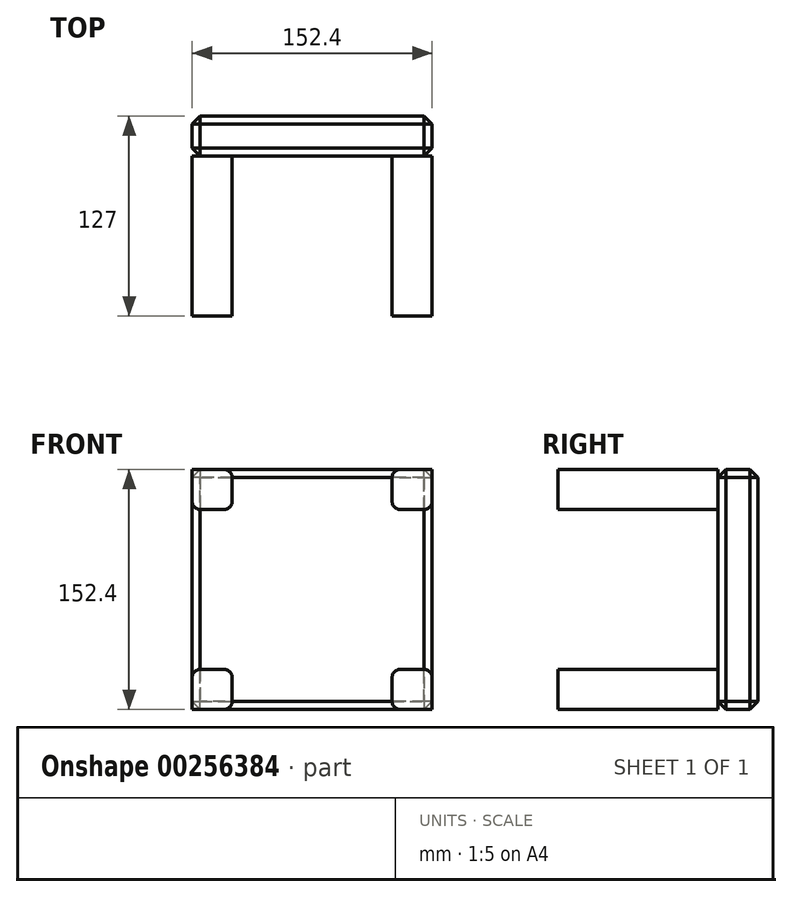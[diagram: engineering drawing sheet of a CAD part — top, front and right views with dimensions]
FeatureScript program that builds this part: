
annotation { "Feature Type Name" : "Feature", "Feature Type Description" : "" }
export const myFeature = defineFeature(function(context is Context, id is Id, definition is map)
    precondition{}
    {
        {
            var Q0;
            Q0=qCreatedBy(makeId("Front.planeOp"),FACE);
            var sketch = newSketch(context, id + "F0", { "sketchPlane" : qUnion([Q0])});
            skLineSegment(sketch, "E0.bottom", {"start": v(-76.2, 76.2) * mm, "end": v(-50.8, 76.2) * mm});
            skLineSegment(sketch, "E0.top", {"start": v(-76.2, 50.8) * mm, "end": v(-50.8, 50.8) * mm});
            skLineSegment(sketch, "E0.left", {"start": v(-76.2, 76.2) * mm, "end": v(-76.2, 50.8) * mm});
            skLineSegment(sketch, "E0.right", {"start": v(-50.8, 76.2) * mm, "end": v(-50.8, 50.8) * mm});
            skLineSegment(sketch, "E1.bottom", {"start": v(76.2, 76.2) * mm, "end": v(50.8, 76.2) * mm});
            skLineSegment(sketch, "E1.top", {"start": v(76.2, 50.8) * mm, "end": v(50.8, 50.8) * mm});
            skLineSegment(sketch, "E1.left", {"start": v(76.2, 76.2) * mm, "end": v(76.2, 50.8) * mm});
            skLineSegment(sketch, "E1.right", {"start": v(50.8, 76.2) * mm, "end": v(50.8, 50.8) * mm});
            skLineSegment(sketch, "E2.bottom", {"start": v(76.2, -76.2) * mm, "end": v(50.8, -76.2) * mm});
            skLineSegment(sketch, "E2.top", {"start": v(76.2, -50.8) * mm, "end": v(50.8, -50.8) * mm});
            skLineSegment(sketch, "E2.left", {"start": v(76.2, -76.2) * mm, "end": v(76.2, -50.8) * mm});
            skLineSegment(sketch, "E2.right", {"start": v(50.8, -76.2) * mm, "end": v(50.8, -50.8) * mm});
            skLineSegment(sketch, "E3.bottom", {"start": v(-76.2, -76.2) * mm, "end": v(-50.8, -76.2) * mm});
            skLineSegment(sketch, "E3.top", {"start": v(-76.2, -50.8) * mm, "end": v(-50.8, -50.8) * mm});
            skLineSegment(sketch, "E3.left", {"start": v(-76.2, -76.2) * mm, "end": v(-76.2, -50.8) * mm});
            skLineSegment(sketch, "E3.right", {"start": v(-50.8, -76.2) * mm, "end": v(-50.8, -50.8) * mm});
            skLineSegment(sketch, "E4.bottom", {"start": v(76.2, 76.2) * mm, "end": v(-76.2, 76.2) * mm});
            skLineSegment(sketch, "E4.top", {"start": v(76.2, -76.2) * mm, "end": v(-76.2, -76.2) * mm});
            skLineSegment(sketch, "E4.left", {"start": v(76.2, 76.2) * mm, "end": v(76.2, -76.2) * mm});
            skLineSegment(sketch, "E4.right", {"start": v(-76.2, 76.2) * mm, "end": v(-76.2, -76.2) * mm});
            skPoint(sketch, "E4.middle", {"position": v(0, 0) * mm});
            skSolve(sketch);
        }
        {
            var Q0;
            {var subQ0=sQuery(id+"F0.wireOp",EDGE,"E0.top");Q0=makeQuery(id+"F0.imprint","IMPRINT",FACE,{"disambiguationData":[TD([[makeQuery(id+"F0.imprint","IMPRINT",EDGE,{"derivedFrom":subQ0}),1.0]])]});}
            var Q1;
            {var subQ0=sQuery(id+"F0.wireOp",EDGE,"E1.top");Q1=makeQuery(id+"F0.imprint","IMPRINT",FACE,{"disambiguationData":[TD([[makeQuery(id+"F0.imprint","IMPRINT",EDGE,{"derivedFrom":subQ0}),-1.0]])]});}
            var Q2;
            {var subQ0=sQuery(id+"F0.wireOp",EDGE,"E2.top");Q2=makeQuery(id+"F0.imprint","IMPRINT",FACE,{"disambiguationData":[TD([[makeQuery(id+"F0.imprint","IMPRINT",EDGE,{"derivedFrom":subQ0}),1.0]])]});}
            var Q3;
            {var subQ0=sQuery(id+"F0.wireOp",EDGE,"E3.top");Q3=makeQuery(id+"F0.imprint","IMPRINT",FACE,{"disambiguationData":[TD([[makeQuery(id+"F0.imprint","IMPRINT",EDGE,{"derivedFrom":subQ0}),-1.0]])]});}
            extrude(context, id + "F1", {"entities" : qUnion([Q0, Q1, Q2, Q3]), "depth" : 101.6 * mm});
        }
        {
            var Q0;
            {var subQ1=sQuery(id+"F0.wireOp",EDGE,"E0.top");Q0=makeQuery(id+"F0.imprint","IMPRINT",FACE,{"disambiguationData":[TD([[makeQuery(id+"F0.imprint","IMPRINT",EDGE,{"derivedFrom":subQ1}),-1.0]])]});}
            var Q1;
            {var subQ0=sQuery(id+"F0.wireOp",EDGE,"E2.top");Q1=makeQuery(id+"F0.imprint","IMPRINT",FACE,{"disambiguationData":[TD([[makeQuery(id+"F0.imprint","IMPRINT",EDGE,{"derivedFrom":subQ0}),1.0]])]});}
            var Q2;
            {var subQ0=sQuery(id+"F0.wireOp",EDGE,"E1.top");Q2=makeQuery(id+"F0.imprint","IMPRINT",FACE,{"disambiguationData":[TD([[makeQuery(id+"F0.imprint","IMPRINT",EDGE,{"derivedFrom":subQ0}),-1.0]])]});}
            var Q3;
            {var subQ0=sQuery(id+"F0.wireOp",EDGE,"E0.top");Q3=makeQuery(id+"F0.imprint","IMPRINT",FACE,{"disambiguationData":[TD([[makeQuery(id+"F0.imprint","IMPRINT",EDGE,{"derivedFrom":subQ0}),1.0]])]});}
            var Q4;
            {var subQ0=sQuery(id+"F0.wireOp",EDGE,"E3.top");Q4=makeQuery(id+"F0.imprint","IMPRINT",FACE,{"disambiguationData":[TD([[makeQuery(id+"F0.imprint","IMPRINT",EDGE,{"derivedFrom":subQ0}),-1.0]])]});}
            extrude(context, id + "F2", {"entities" : qUnion([Q0, Q1, Q2, Q3, Q4]), "oppositeDirection" : true, "depth" : 25.4 * mm});
        }
        {
            var Q0;
            Q0=makeQuery(id+"F1.opExtrude","SWEPT_EDGE",EDGE,{"disambiguationData":[OSD([sQuery(id+"F0.wireOp",EDGE,"E2.top"),sQuery(id+"F0.wireOp",EDGE,"E4.left")])]});
            var Q1;
            Q1=makeQuery(id+"F1.opExtrude","SWEPT_EDGE",EDGE,{"disambiguationData":[OSD([sQuery(id+"F0.wireOp",EDGE,"E4.top"),sQuery(id+"F0.wireOp",EDGE,"E4.left")])]});
            var Q2;
            Q2=makeQuery(id+"F1.opExtrude","SWEPT_EDGE",EDGE,{"disambiguationData":[OSD([sQuery(id+"F0.wireOp",EDGE,"E2.right"),sQuery(id+"F0.wireOp",EDGE,"E4.top")])]});
            var Q3;
            Q3=makeQuery(id+"F1.opExtrude","SWEPT_EDGE",EDGE,{"disambiguationData":[OSD([sQuery(id+"F0.wireOp",EDGE,"E2.top"),sQuery(id+"F0.wireOp",EDGE,"E2.right")])]});
            fillet(context, id + "F3", {"entities" : qUnion([Q0, Q1, Q2, Q3]), "radius" : 5.08 * mm, "tangentPropagation" : true, "allowEdgeOverflow" : false});
        }
        {
            var Q0;
            Q0=makeQuery(id+"F1.opExtrude","SWEPT_EDGE",EDGE,{"disambiguationData":[OSD([sQuery(id+"F0.wireOp",EDGE,"E4.top"),sQuery(id+"F0.wireOp",EDGE,"E4.right")])]});
            var Q1;
            Q1=makeQuery(id+"F1.opExtrude","SWEPT_EDGE",EDGE,{"disambiguationData":[OSD([sQuery(id+"F0.wireOp",EDGE,"E3.top"),sQuery(id+"F0.wireOp",EDGE,"E4.right")])]});
            var Q2;
            Q2=makeQuery(id+"F1.opExtrude","SWEPT_EDGE",EDGE,{"disambiguationData":[OSD([sQuery(id+"F0.wireOp",EDGE,"E3.right"),sQuery(id+"F0.wireOp",EDGE,"E4.top")])]});
            var Q3;
            Q3=makeQuery(id+"F1.opExtrude","SWEPT_EDGE",EDGE,{"disambiguationData":[OSD([sQuery(id+"F0.wireOp",EDGE,"E3.top"),sQuery(id+"F0.wireOp",EDGE,"E3.right")])]});
            fillet(context, id + "F4", {"entities" : qUnion([Q0, Q1, Q2, Q3]), "radius" : 5.08 * mm, "tangentPropagation" : true, "allowEdgeOverflow" : false});
        }
        {
            var Q0;
            Q0=makeQuery(id+"F1.opExtrude","SWEPT_EDGE",EDGE,{"disambiguationData":[OSD([sQuery(id+"F0.wireOp",EDGE,"E1.top"),sQuery(id+"F0.wireOp",EDGE,"E4.left")])]});
            var Q1;
            Q1=makeQuery(id+"F1.opExtrude","SWEPT_EDGE",EDGE,{"disambiguationData":[OSD([sQuery(id+"F0.wireOp",EDGE,"E1.top"),sQuery(id+"F0.wireOp",EDGE,"E1.right")])]});
            var Q2;
            Q2=makeQuery(id+"F1.opExtrude","SWEPT_EDGE",EDGE,{"disambiguationData":[OSD([sQuery(id+"F0.wireOp",EDGE,"E4.bottom"),sQuery(id+"F0.wireOp",EDGE,"E4.left")])]});
            var Q3;
            Q3=makeQuery(id+"F1.opExtrude","SWEPT_EDGE",EDGE,{"disambiguationData":[OSD([sQuery(id+"F0.wireOp",EDGE,"E1.right"),sQuery(id+"F0.wireOp",EDGE,"E4.bottom")])]});
            fillet(context, id + "F5", {"entities" : qUnion([Q0, Q1, Q2, Q3]), "radius" : 5.08 * mm, "tangentPropagation" : true, "allowEdgeOverflow" : false});
        }
        {
            var Q0;
            Q0=makeQuery(id+"F1.opExtrude","SWEPT_EDGE",EDGE,{"disambiguationData":[OSD([sQuery(id+"F0.wireOp",EDGE,"E4.bottom"),sQuery(id+"F0.wireOp",EDGE,"E4.right")])]});
            var Q1;
            Q1=makeQuery(id+"F1.opExtrude","SWEPT_EDGE",EDGE,{"disambiguationData":[OSD([sQuery(id+"F0.wireOp",EDGE,"E0.right"),sQuery(id+"F0.wireOp",EDGE,"E4.bottom")])]});
            var Q2;
            Q2=makeQuery(id+"F1.opExtrude","SWEPT_EDGE",EDGE,{"disambiguationData":[OSD([sQuery(id+"F0.wireOp",EDGE,"E0.top"),sQuery(id+"F0.wireOp",EDGE,"E0.right")])]});
            var Q3;
            Q3=makeQuery(id+"F1.opExtrude","SWEPT_EDGE",EDGE,{"disambiguationData":[OSD([sQuery(id+"F0.wireOp",EDGE,"E0.top"),sQuery(id+"F0.wireOp",EDGE,"E4.right")])]});
            fillet(context, id + "F6", {"entities" : qUnion([Q0, Q1, Q2, Q3]), "radius" : 5.08 * mm, "tangentPropagation" : true, "allowEdgeOverflow" : false});
        }
        {
            var Q0;
            Q0=makeQuery(id+"F2.opExtrude","SWEPT_FACE",FACE,{"disambiguationData":[OSD([sQuery(id+"F0.wireOp",EDGE,"E4.top")])]});
            var Q1;
            Q1=makeQuery(id+"F2.opExtrude","SWEPT_FACE",FACE,{"disambiguationData":[OSD([sQuery(id+"F0.wireOp",EDGE,"E4.left")])]});
            var Q2;
            Q2=makeQuery(id+"F2.opExtrude","SWEPT_FACE",FACE,{"disambiguationData":[OSD([sQuery(id+"F0.wireOp",EDGE,"E4.bottom")])]});
            var Q3;
            Q3=makeQuery(id+"F2.opExtrude","SWEPT_FACE",FACE,{"disambiguationData":[OSD([sQuery(id+"F0.wireOp",EDGE,"E4.right")])]});
            chamfer(context, id + "F7", {"entities" : qUnion([Q0, Q1, Q2, Q3]), "width" : 5.08 * mm, "tangentPropagation" : true});
        }
    });
